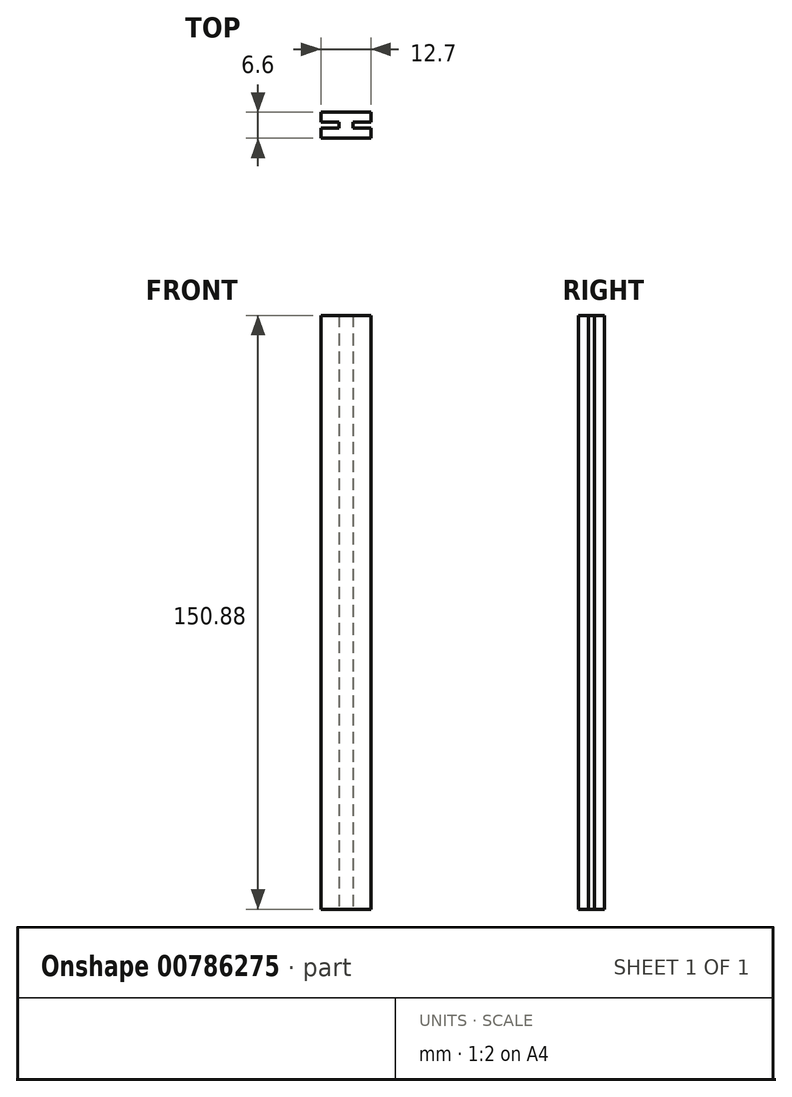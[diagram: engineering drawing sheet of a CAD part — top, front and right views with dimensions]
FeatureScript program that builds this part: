
annotation { "Feature Type Name" : "Feature", "Feature Type Description" : "" }
export const myFeature = defineFeature(function(context is Context, id is Id, definition is map)
    precondition{}
    {
        {
            var Q0;
            Q0=qCreatedBy(makeId("Top.planeOp"),FACE);
            var sketch = newSketch(context, id + "F0", { "sketchPlane" : qUnion([Q0])});
            skLineSegment(sketch, "E0.bottom", {"start": v(0, 0) * mm, "end": v(12.7, 0) * mm});
            skLineSegment(sketch, "E0.top", {"start": v(0, -6.6) * mm, "end": v(12.7, -6.6) * mm});
            skLineSegment(sketch, "E0.left", {"start": v(0, 0) * mm, "end": v(0, -2.54) * mm});
            skLineSegment(sketch, "E0.right", {"start": v(12.7, 0) * mm, "end": v(12.7, -2.54) * mm});
            skLineSegment(sketch, "E1.bottom", {"start": v(0, -2.54) * mm, "end": v(4.57, -2.54) * mm});
            skLineSegment(sketch, "E1.top", {"start": v(0, -4.06) * mm, "end": v(4.57, -4.06) * mm});
            skLineSegment(sketch, "E1.right", {"start": v(4.57, -2.54) * mm, "end": v(4.57, -4.06) * mm});
            skLineSegment(sketch, "E2.bottom", {"start": v(12.7, -2.54) * mm, "end": v(8.13, -2.54) * mm});
            skLineSegment(sketch, "E2.top", {"start": v(12.7, -4.06) * mm, "end": v(8.13, -4.06) * mm});
            skLineSegment(sketch, "E2.right", {"start": v(8.13, -2.54) * mm, "end": v(8.13, -4.06) * mm});
            skLineSegment(sketch, "E3.trimOffspring", {"start": v(0, -4.06) * mm, "end": v(0, -6.6) * mm});
            skLineSegment(sketch, "E4.trimOffspring", {"start": v(12.7, -4.06) * mm, "end": v(12.7, -6.6) * mm});
            skSolve(sketch);
        }
        {
            var Q0;
            Q0 = qSketchRegion(id + "F0", true);
            extrude(context, id + "F1", {"entities" : qUnion([Q0]), "depth" : 150.88 * mm, "offsetDistance" : 25.4 * mm});
        }
    });
